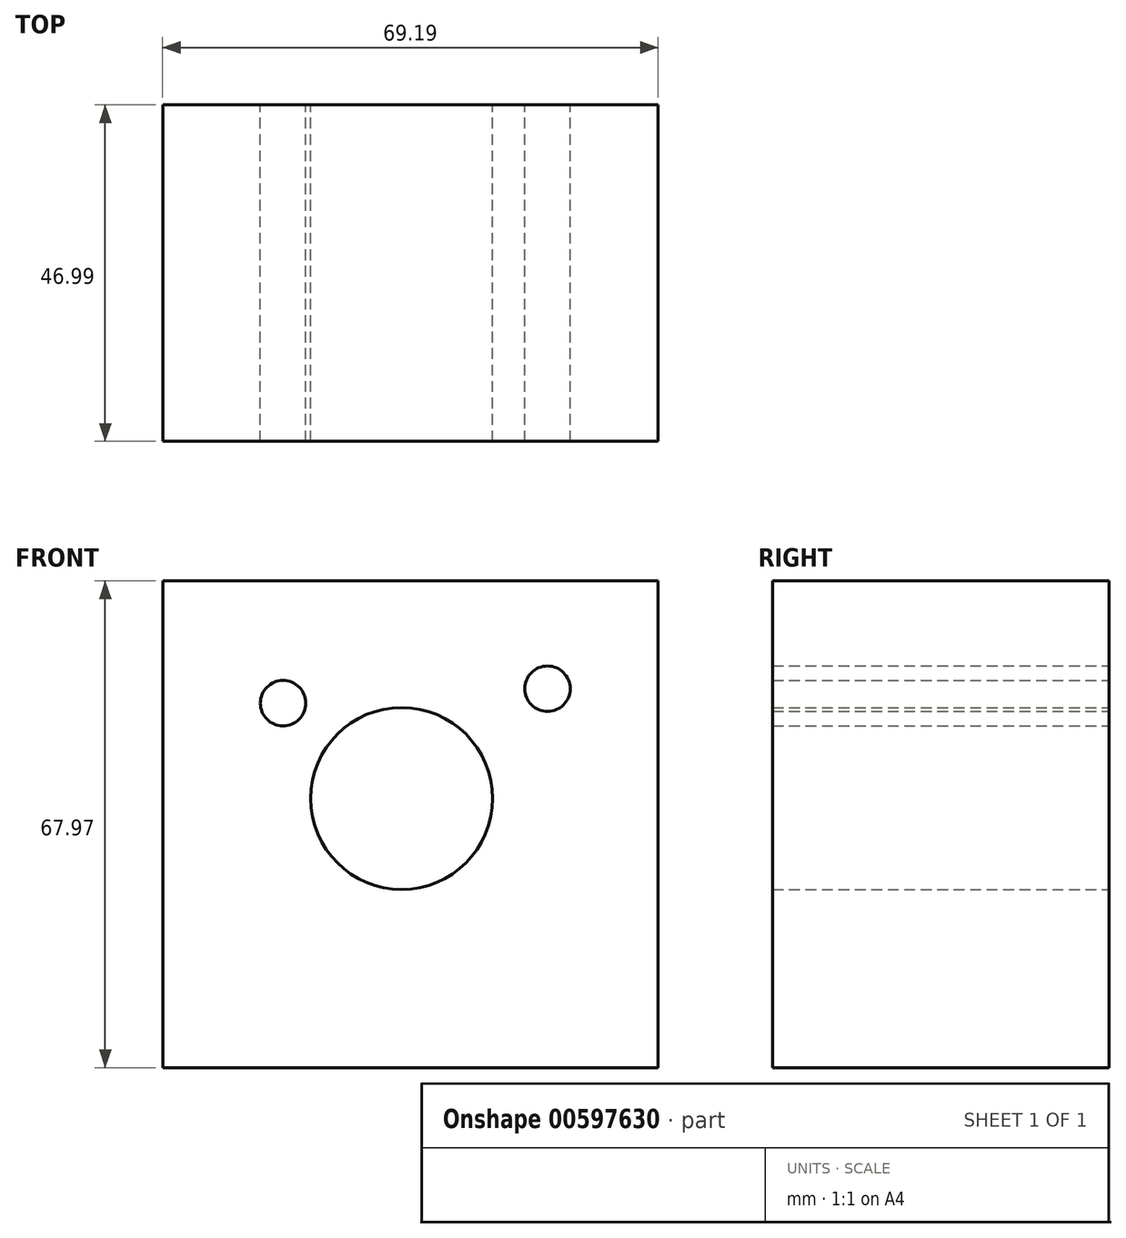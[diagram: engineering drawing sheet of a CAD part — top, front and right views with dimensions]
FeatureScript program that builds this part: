
annotation { "Feature Type Name" : "Feature", "Feature Type Description" : "" }
export const myFeature = defineFeature(function(context is Context, id is Id, definition is map)
    precondition{}
    {
        {
            var Q0;
            Q0=qCreatedBy(makeId("Front.planeOp"),FACE);
            var sketch = newSketch(context, id + "F0", { "sketchPlane" : qUnion([Q0])});
            skLineSegment(sketch, "E0.bottom", {"start": v(-33.38, 36.88) * mm, "end": v(35.81, 36.88) * mm});
            skLineSegment(sketch, "E0.top", {"start": v(-33.38, -31.09) * mm, "end": v(35.81, -31.09) * mm});
            skLineSegment(sketch, "E0.left", {"start": v(-33.38, 36.88) * mm, "end": v(-33.38, -31.09) * mm});
            skLineSegment(sketch, "E0.right", {"start": v(35.81, 36.88) * mm, "end": v(35.81, -31.09) * mm});
            skSolve(sketch);
        }
        {
            var Q0;
            Q0=makeQuery(id+"F0.imprint","IMPRINT",FACE,{"disambiguationData":[TD([[makeQuery(id+"F0.imprint","IMPRINT",EDGE,{"derivedFrom":sQuery(id+"F0.wireOp",EDGE,"E0.bottom")}),-1.0]])]});
            extrude(context, id + "F1", {"entities" : qUnion([Q0]), "depth" : 47 * mm, "offsetDistance" : 25.4 * mm});
        }
        {
            var Q0;
            Q0=makeQuery(id+"F1.opExtrude","CAP_FACE",FACE,{"disambiguationData":[OSD([sQuery(id+"F0.wireOp",EDGE,"E0.bottom"),sQuery(id+"F0.wireOp",EDGE,"E0.top"),sQuery(id+"F0.wireOp",EDGE,"E0.left"),sQuery(id+"F0.wireOp",EDGE,"E0.right")])],"isStart":true});
            var sketch = newSketch(context, id + "F2", { "sketchPlane" : qUnion([Q0])});
            skPoint(sketch, "E1", {"position": v(0, 6.5) * mm});
            skSolve(sketch);
        }
        {
            var Q0;
            Q0=makeQuery(id+"F2.imprint","IMPRINT",FACE,{"disambiguationData":[TD([[makeQuery(id+"F2.imprint","IMPRINT",EDGE,{"derivedFrom":makeQuery(id+"F1.opExtrude","CAP_EDGE",EDGE,{"disambiguationData":[OSD([sQuery(id+"F0.wireOp",EDGE,"E0.bottom")])],"isStart":true})}),1.0]])]});
            var sketch = newSketch(context, id + "F3", { "sketchPlane" : qUnion([Q0])});
            skPoint(sketch, "E2", {"position": v(-20.37, 21.82) * mm});
            skPoint(sketch, "E3", {"position": v(16.56, 19.8) * mm});
            skSolve(sketch);
        }
        {
            var Q0;
            Q0=sQuery(id+"F2.wireOp",VERTEX,"E1");
            var Q1;
            Q1=makeQuery(id+"F1.opExtrude","SWEPT_BODY",BODY,{"disambiguationData":[OSD([sQuery(id+"F0.wireOp",EDGE,"E0.bottom"),sQuery(id+"F0.wireOp",EDGE,"E0.top"),sQuery(id+"F0.wireOp",EDGE,"E0.left"),sQuery(id+"F0.wireOp",EDGE,"E0.right")])]});
            hole(context, id + "F4", {"style" : HoleStyle.SIMPLE, "endStyle" : HoleEndStyle.THROUGH, "holeDiameter" : 25.4 * mm, "majorDiameter" : 6.35 * mm, "isTappedThrough" : true, "tappedDepth" : 12.7 * mm, "tapClearance" : 3, "locations" : qUnion([Q0]), "scope" : qUnion([Q1])});
        }
        {
            var Q0;
            Q0=sQuery(id+"F3.wireOp",VERTEX,"E2");
            var Q1;
            Q1=makeQuery(id+"F1.opExtrude","SWEPT_BODY",BODY,{"disambiguationData":[OSD([sQuery(id+"F0.wireOp",EDGE,"E0.bottom"),sQuery(id+"F0.wireOp",EDGE,"E0.top"),sQuery(id+"F0.wireOp",EDGE,"E0.left"),sQuery(id+"F0.wireOp",EDGE,"E0.right")])]});
            hole(context, id + "F5", {"style" : HoleStyle.SIMPLE, "endStyle" : HoleEndStyle.THROUGH, "holeDiameter" : 6.35 * mm, "majorDiameter" : 6.35 * mm, "isTappedThrough" : true, "tappedDepth" : 12.7 * mm, "tapClearance" : 3, "locations" : qUnion([Q0]), "scope" : qUnion([Q1])});
        }
        {
            var Q0;
            Q0=sQuery(id+"F3.wireOp",VERTEX,"E3");
            var Q1;
            Q1=makeQuery(id+"F1.opExtrude","SWEPT_BODY",BODY,{"disambiguationData":[OSD([sQuery(id+"F0.wireOp",EDGE,"E0.bottom"),sQuery(id+"F0.wireOp",EDGE,"E0.top"),sQuery(id+"F0.wireOp",EDGE,"E0.left"),sQuery(id+"F0.wireOp",EDGE,"E0.right")])]});
            hole(context, id + "F6", {"style" : HoleStyle.SIMPLE, "endStyle" : HoleEndStyle.THROUGH, "holeDiameter" : 6.35 * mm, "majorDiameter" : 6.35 * mm, "isTappedThrough" : true, "tappedDepth" : 12.7 * mm, "tapClearance" : 3, "locations" : qUnion([Q0]), "scope" : qUnion([Q1])});
        }
    });
